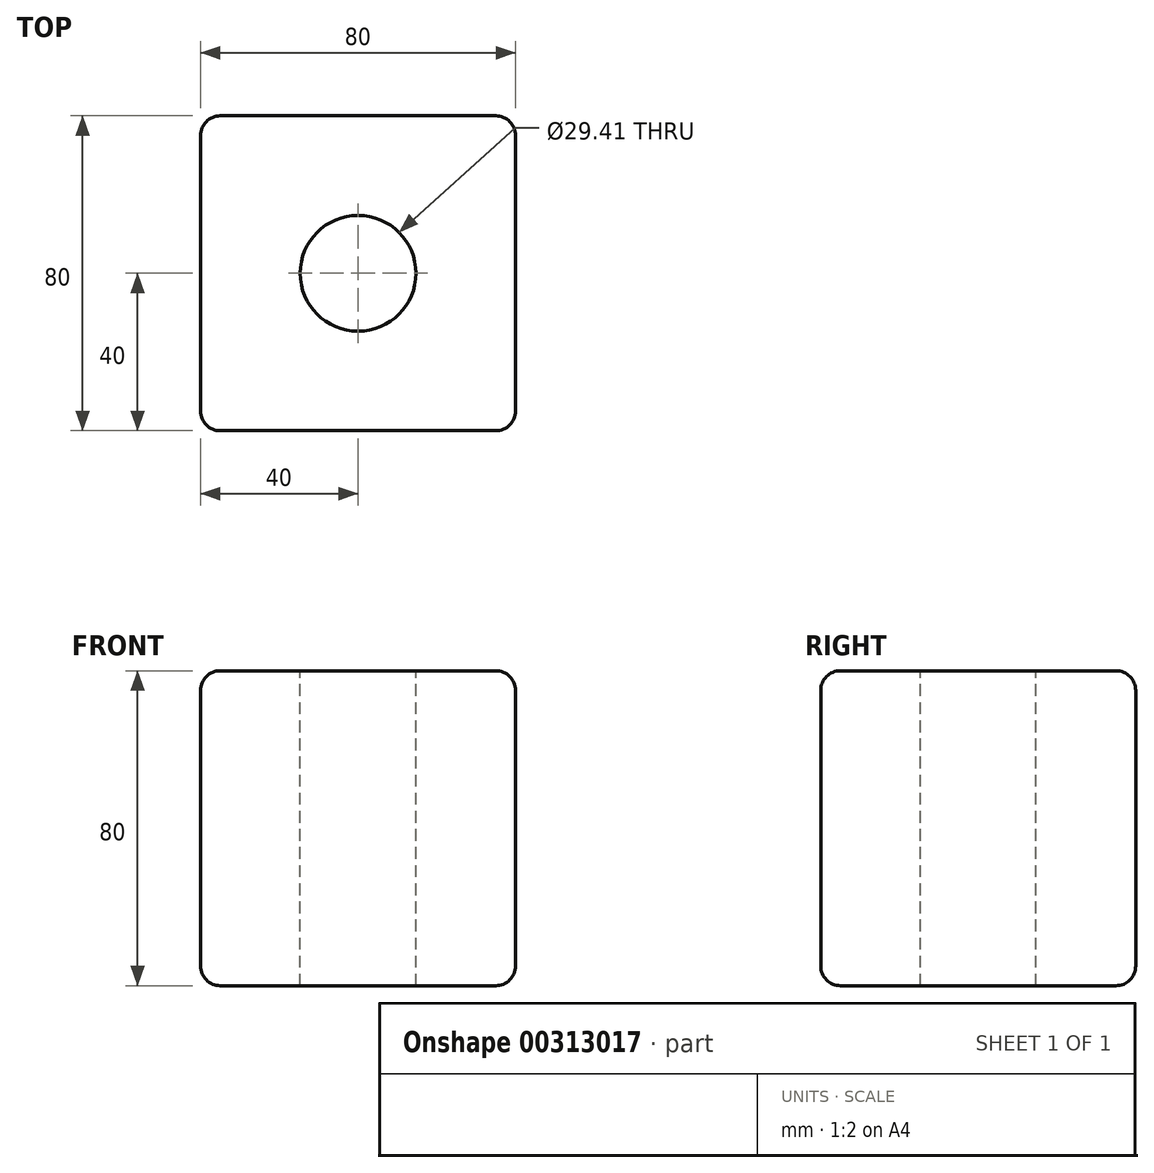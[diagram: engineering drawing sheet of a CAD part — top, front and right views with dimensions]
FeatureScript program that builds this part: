
annotation { "Feature Type Name" : "Feature", "Feature Type Description" : "" }
export const myFeature = defineFeature(function(context is Context, id is Id, definition is map)
    precondition{}
    {
        {
            var Q0;
            Q0=qCreatedBy(makeId("Top.planeOp"),FACE);
            var sketch = newSketch(context, id + "F0", { "sketchPlane" : qUnion([Q0])});
            skLineSegment(sketch, "E0.bottom", {"start": v(-40, 40) * mm, "end": v(40, 40) * mm});
            skLineSegment(sketch, "E0.top", {"start": v(-40, -40) * mm, "end": v(40, -40) * mm});
            skLineSegment(sketch, "E0.left", {"start": v(-40, 40) * mm, "end": v(-40, -40) * mm});
            skLineSegment(sketch, "E0.right", {"start": v(40, 40) * mm, "end": v(40, -40) * mm});
            skPoint(sketch, "E0.middle", {"position": v(0, 0) * mm});
            skSolve(sketch);
        }
        {
            var Q0;
            Q0=makeQuery(id+"F0.imprint","IMPRINT",FACE,{"disambiguationData":[TD([[makeQuery(id+"F0.imprint","IMPRINT",EDGE,{"derivedFrom":sQuery(id+"F0.wireOp",EDGE,"E0.bottom")}),-1.0]])]});
            extrude(context, id + "F1", {"entities" : qUnion([Q0]), "endBound" : BoundingType.SYMMETRIC, "depth" : 80 * mm});
        }
        {
            var Q0;
            Q0=makeQuery(id+"F1.opExtrude","CAP_EDGE",EDGE,{"disambiguationData":[OSD([sQuery(id+"F0.wireOp",EDGE,"E0.bottom")])],"isStart":true});
            var Q1;
            Q1=makeQuery(id+"F1.opExtrude","CAP_EDGE",EDGE,{"disambiguationData":[OSD([sQuery(id+"F0.wireOp",EDGE,"E0.top")])],"isStart":true});
            var Q2;
            Q2=makeQuery(id+"F1.opExtrude","CAP_EDGE",EDGE,{"disambiguationData":[OSD([sQuery(id+"F0.wireOp",EDGE,"E0.left")])],"isStart":true});
            var Q3;
            Q3=makeQuery(id+"F1.opExtrude","CAP_EDGE",EDGE,{"disambiguationData":[OSD([sQuery(id+"F0.wireOp",EDGE,"E0.right")])],"isStart":true});
            var Q4;
            Q4=makeQuery(id+"F1.opExtrude","SWEPT_EDGE",EDGE,{"disambiguationData":[OSD([sQuery(id+"F0.wireOp",EDGE,"E0.bottom"),sQuery(id+"F0.wireOp",EDGE,"E0.right")])]});
            var Q5;
            Q5=makeQuery(id+"F1.opExtrude","SWEPT_EDGE",EDGE,{"disambiguationData":[OSD([sQuery(id+"F0.wireOp",EDGE,"E0.top"),sQuery(id+"F0.wireOp",EDGE,"E0.left")])]});
            var Q6;
            Q6=makeQuery(id+"F1.opExtrude","CAP_FACE",FACE,{"disambiguationData":[OSD([sQuery(id+"F0.wireOp",EDGE,"E0.bottom"),sQuery(id+"F0.wireOp",EDGE,"E0.top"),sQuery(id+"F0.wireOp",EDGE,"E0.left"),sQuery(id+"F0.wireOp",EDGE,"E0.right")])],"isStart":false});
            var Q7;
            Q7=makeQuery(id+"F1.opExtrude","SWEPT_EDGE",EDGE,{"disambiguationData":[OSD([sQuery(id+"F0.wireOp",EDGE,"E0.top"),sQuery(id+"F0.wireOp",EDGE,"E0.right")])]});
            var Q8;
            Q8=makeQuery(id+"F1.opExtrude","SWEPT_EDGE",EDGE,{"disambiguationData":[OSD([sQuery(id+"F0.wireOp",EDGE,"E0.bottom"),sQuery(id+"F0.wireOp",EDGE,"E0.left")])]});
            var Q9;
            Q9=makeQuery(id+"F1.opExtrude","SWEPT_FACE",FACE,{"disambiguationData":[OSD([sQuery(id+"F0.wireOp",EDGE,"E0.left")])]});
            var Q10;
            Q10=makeQuery(id+"F1.opExtrude","CAP_FACE",FACE,{"disambiguationData":[OSD([sQuery(id+"F0.wireOp",EDGE,"E0.bottom"),sQuery(id+"F0.wireOp",EDGE,"E0.top"),sQuery(id+"F0.wireOp",EDGE,"E0.left"),sQuery(id+"F0.wireOp",EDGE,"E0.right")])],"isStart":true});
            var Q11;
            Q11=makeQuery(id+"F1.opExtrude","SWEPT_FACE",FACE,{"disambiguationData":[OSD([sQuery(id+"F0.wireOp",EDGE,"E0.bottom")])]});
            fillet(context, id + "F2", {"entities" : qUnion([Q0, Q1, Q2, Q3, Q4, Q5, Q6, Q7, Q8, Q9, Q10, Q11]), "radius" : 5 * mm, "tangentPropagation" : true, "allowEdgeOverflow" : false});
        }
        {
            var Q0;
            Q0=makeQuery(id+"F1.opExtrude","CAP_FACE",FACE,{"disambiguationData":[OSD([sQuery(id+"F0.wireOp",EDGE,"E0.bottom"),sQuery(id+"F0.wireOp",EDGE,"E0.top"),sQuery(id+"F0.wireOp",EDGE,"E0.left"),sQuery(id+"F0.wireOp",EDGE,"E0.right")])],"isStart":false});
            var sketch = newSketch(context, id + "F3", { "sketchPlane" : qUnion([Q0])});
            skCircle(sketch, "E1", {"center": v(0, 0) * mm, "radius": 14.7 * mm});
            skSolve(sketch);
        }
        {
            var Q0;
            Q0=makeQuery(id+"F3.imprint","IMPRINT",FACE,{"disambiguationData":[TD([[makeQuery(id+"F3.imprint","IMPRINT",EDGE,{"derivedFrom":sQuery(id+"F3.wireOp",EDGE,"E1")}),1.0]])]});
            extrude(context, id + "F4", {"entities" : qUnion([Q0]), "operationType" : NewBodyOperationType.REMOVE, "endBound" : BoundingType.THROUGH_ALL, "oppositeDirection" : true, "depth" : 25 * mm});
        }
    });
